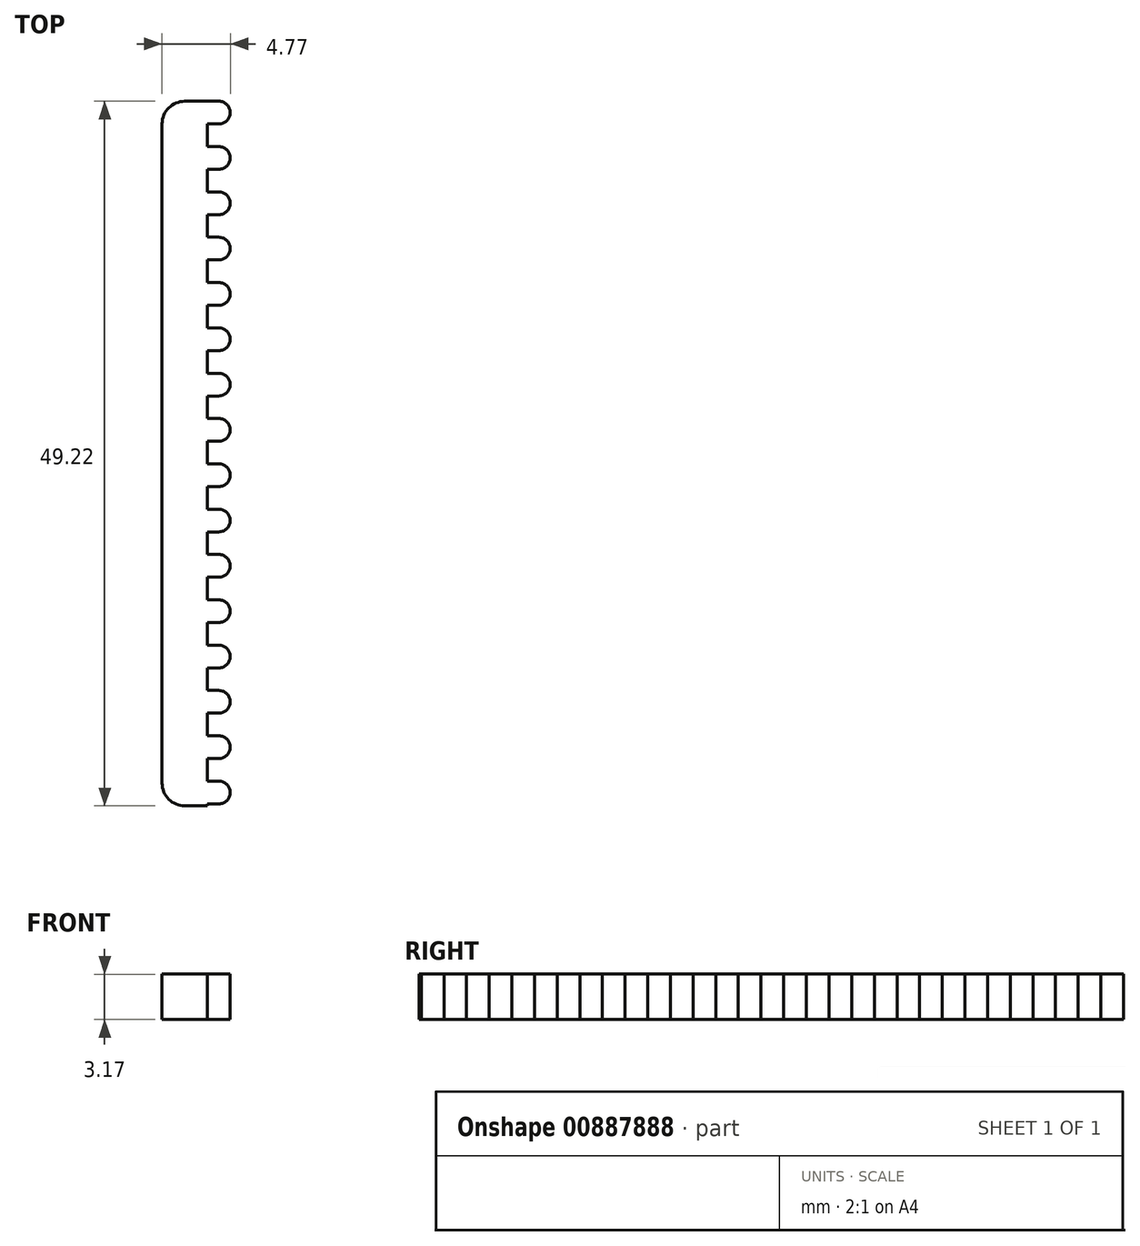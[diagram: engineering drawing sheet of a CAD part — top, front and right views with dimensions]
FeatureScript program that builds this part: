
annotation { "Feature Type Name" : "Feature", "Feature Type Description" : "" }
export const myFeature = defineFeature(function(context is Context, id is Id, definition is map)
    precondition{}
    {
        {
            var Q0;
            Q0=qCreatedBy(makeId("Top.planeOp"),FACE);
            var sketch = newSketch(context, id + "F0", { "sketchPlane" : qUnion([Q0])});
            skLineSegment(sketch, "E0.bottom", {"start": v(-12.7, -24.6) * mm, "end": v(-15.88, -24.6) * mm});
            skLineSegment(sketch, "E0.top", {"start": v(-12.7, 24.6) * mm, "end": v(-15.88, 24.6) * mm});
            skLineSegment(sketch, "E0.left", {"start": v(-12.7, -24.6) * mm, "end": v(-12.7, 24.6) * mm});
            skLineSegment(sketch, "E0.right", {"start": v(-15.88, -24.6) * mm, "end": v(-15.88, 24.6) * mm});
            skPoint(sketch, "E0.middle", {"position": v(-14.29, 0) * mm});
            skLineSegment(sketch, "E1.bottom", {"start": v(-12.7, 24.6) * mm, "end": v(-11.9, 24.6) * mm});
            skLineSegment(sketch, "E1.top", {"start": v(-12.7, 23.02) * mm, "end": v(-11.9, 23.02) * mm});
            skLineSegment(sketch, "E1.left", {"start": v(-12.7, 24.6) * mm, "end": v(-12.7, 23.02) * mm});
            skLineSegment(sketch, "E1.right", {"start": v(-11.11, 23.81) * mm, "end": v(-11.11, 23.81) * mm});
            skPoint(sketch, "E2.visualSharp", {"position": v(-11.11, 24.6) * mm});
            skArc(sketch, "E2.filletArc", {"start": v(-11.11, 23.81) * mm, "mid": v(-11.34, 24.37) * mm, "end": v(-11.9, 24.6) * mm});
            skPoint(sketch, "E3.visualSharp", {"position": v(-11.11, 23.02) * mm});
            skArc(sketch, "E3.filletArc", {"start": v(-11.9, 23.02) * mm, "mid": v(-11.34, 23.25) * mm, "end": v(-11.11, 23.81) * mm});
            skLineSegment(sketch, "E4.1.0.0", {"start": v(-12.7, 21.44) * mm, "end": v(-11.9, 21.44) * mm});
            skArc(sketch, "E4.1.0.1", {"start": v(-11.11, 20.65) * mm, "mid": v(-11.34, 21.2) * mm, "end": v(-11.9, 21.44) * mm});
            skArc(sketch, "E4.1.0.2", {"start": v(-11.9, 19.85) * mm, "mid": v(-11.34, 20.09) * mm, "end": v(-11.11, 20.65) * mm});
            skLineSegment(sketch, "E4.1.0.3", {"start": v(-12.7, 19.85) * mm, "end": v(-11.9, 19.85) * mm});
            skLineSegment(sketch, "E4.2.0.0", {"start": v(-12.7, 18.28) * mm, "end": v(-11.9, 18.28) * mm});
            skArc(sketch, "E4.2.0.1", {"start": v(-11.11, 17.48) * mm, "mid": v(-11.34, 18.04) * mm, "end": v(-11.9, 18.28) * mm});
            skArc(sketch, "E4.2.0.2", {"start": v(-11.9, 16.69) * mm, "mid": v(-11.34, 16.92) * mm, "end": v(-11.11, 17.48) * mm});
            skLineSegment(sketch, "E4.2.0.3", {"start": v(-12.7, 16.69) * mm, "end": v(-11.9, 16.69) * mm});
            skLineSegment(sketch, "E4.3.0.0", {"start": v(-12.7, 15.1) * mm, "end": v(-11.9, 15.1) * mm});
            skArc(sketch, "E4.3.0.1", {"start": v(-11.11, 14.32) * mm, "mid": v(-11.34, 14.88) * mm, "end": v(-11.9, 15.1) * mm});
            skArc(sketch, "E4.3.0.2", {"start": v(-11.9, 13.52) * mm, "mid": v(-11.34, 13.75) * mm, "end": v(-11.11, 14.32) * mm});
            skLineSegment(sketch, "E4.3.0.3", {"start": v(-12.7, 13.52) * mm, "end": v(-11.9, 13.52) * mm});
            skLineSegment(sketch, "E4.4.0.0", {"start": v(-12.7, 11.94) * mm, "end": v(-11.9, 11.94) * mm});
            skArc(sketch, "E4.4.0.1", {"start": v(-11.11, 11.15) * mm, "mid": v(-11.34, 11.71) * mm, "end": v(-11.9, 11.94) * mm});
            skArc(sketch, "E4.4.0.2", {"start": v(-11.9, 10.36) * mm, "mid": v(-11.34, 10.59) * mm, "end": v(-11.11, 11.15) * mm});
            skLineSegment(sketch, "E4.4.0.3", {"start": v(-12.7, 10.36) * mm, "end": v(-11.9, 10.36) * mm});
            skLineSegment(sketch, "E4.5.0.0", {"start": v(-12.7, 8.78) * mm, "end": v(-11.9, 8.78) * mm});
            skArc(sketch, "E4.5.0.1", {"start": v(-11.11, 7.99) * mm, "mid": v(-11.34, 8.55) * mm, "end": v(-11.9, 8.78) * mm});
            skArc(sketch, "E4.5.0.2", {"start": v(-11.9, 7.2) * mm, "mid": v(-11.34, 7.42) * mm, "end": v(-11.11, 7.99) * mm});
            skLineSegment(sketch, "E4.5.0.3", {"start": v(-12.7, 7.2) * mm, "end": v(-11.9, 7.2) * mm});
            skLineSegment(sketch, "E4.6.0.0", {"start": v(-12.7, 5.61) * mm, "end": v(-11.9, 5.61) * mm});
            skArc(sketch, "E4.6.0.1", {"start": v(-11.11, 4.82) * mm, "mid": v(-11.34, 5.38) * mm, "end": v(-11.9, 5.61) * mm});
            skArc(sketch, "E4.6.0.2", {"start": v(-11.9, 4.03) * mm, "mid": v(-11.34, 4.26) * mm, "end": v(-11.11, 4.82) * mm});
            skLineSegment(sketch, "E4.6.0.3", {"start": v(-12.7, 4.03) * mm, "end": v(-11.9, 4.03) * mm});
            skLineSegment(sketch, "E4.7.0.0", {"start": v(-12.7, 2.45) * mm, "end": v(-11.9, 2.45) * mm});
            skArc(sketch, "E4.7.0.1", {"start": v(-11.11, 1.65) * mm, "mid": v(-11.34, 2.22) * mm, "end": v(-11.9, 2.45) * mm});
            skArc(sketch, "E4.7.0.2", {"start": v(-11.9, 0.86) * mm, "mid": v(-11.34, 1.1) * mm, "end": v(-11.11, 1.65) * mm});
            skLineSegment(sketch, "E4.7.0.3", {"start": v(-12.7, 0.86) * mm, "end": v(-11.9, 0.86) * mm});
            skLineSegment(sketch, "E4.8.0.0", {"start": v(-12.7, -0.72) * mm, "end": v(-11.9, -0.72) * mm});
            skArc(sketch, "E4.8.0.1", {"start": v(-11.11, -1.51) * mm, "mid": v(-11.34, -0.95) * mm, "end": v(-11.9, -0.72) * mm});
            skArc(sketch, "E4.8.0.2", {"start": v(-11.9, -2.3) * mm, "mid": v(-11.34, -2.07) * mm, "end": v(-11.11, -1.51) * mm});
            skLineSegment(sketch, "E4.8.0.3", {"start": v(-12.7, -2.3) * mm, "end": v(-11.9, -2.3) * mm});
            skLineSegment(sketch, "E4.9.0.0", {"start": v(-12.7, -3.88) * mm, "end": v(-11.9, -3.88) * mm});
            skArc(sketch, "E4.9.0.1", {"start": v(-11.11, -4.68) * mm, "mid": v(-11.34, -4.12) * mm, "end": v(-11.9, -3.88) * mm});
            skArc(sketch, "E4.9.0.2", {"start": v(-11.9, -5.47) * mm, "mid": v(-11.34, -5.24) * mm, "end": v(-11.11, -4.68) * mm});
            skLineSegment(sketch, "E4.9.0.3", {"start": v(-12.7, -5.47) * mm, "end": v(-11.9, -5.47) * mm});
            skLineSegment(sketch, "E4.10.0.0", {"start": v(-12.7, -7.05) * mm, "end": v(-11.9, -7.05) * mm});
            skArc(sketch, "E4.10.0.1", {"start": v(-11.11, -7.84) * mm, "mid": v(-11.34, -7.28) * mm, "end": v(-11.9, -7.05) * mm});
            skArc(sketch, "E4.10.0.2", {"start": v(-11.9, -8.64) * mm, "mid": v(-11.34, -8.4) * mm, "end": v(-11.11, -7.84) * mm});
            skLineSegment(sketch, "E4.10.0.3", {"start": v(-12.7, -8.64) * mm, "end": v(-11.9, -8.64) * mm});
            skLineSegment(sketch, "E4.11.0.0", {"start": v(-12.7, -10.21) * mm, "end": v(-11.9, -10.21) * mm});
            skArc(sketch, "E4.11.0.1", {"start": v(-11.11, -11) * mm, "mid": v(-11.34, -10.45) * mm, "end": v(-11.9, -10.21) * mm});
            skArc(sketch, "E4.11.0.2", {"start": v(-11.9, -11.8) * mm, "mid": v(-11.34, -11.57) * mm, "end": v(-11.11, -11) * mm});
            skLineSegment(sketch, "E4.11.0.3", {"start": v(-12.7, -11.8) * mm, "end": v(-11.9, -11.8) * mm});
            skLineSegment(sketch, "E4.12.0.0", {"start": v(-12.7, -13.38) * mm, "end": v(-11.9, -13.38) * mm});
            skArc(sketch, "E4.12.0.1", {"start": v(-11.11, -14.17) * mm, "mid": v(-11.34, -13.61) * mm, "end": v(-11.9, -13.38) * mm});
            skArc(sketch, "E4.12.0.2", {"start": v(-11.9, -14.97) * mm, "mid": v(-11.34, -14.73) * mm, "end": v(-11.11, -14.17) * mm});
            skLineSegment(sketch, "E4.12.0.3", {"start": v(-12.7, -14.97) * mm, "end": v(-11.9, -14.97) * mm});
            skLineSegment(sketch, "E4.13.0.0", {"start": v(-12.7, -16.55) * mm, "end": v(-11.9, -16.55) * mm});
            skArc(sketch, "E4.13.0.1", {"start": v(-11.11, -17.34) * mm, "mid": v(-11.34, -16.78) * mm, "end": v(-11.9, -16.55) * mm});
            skArc(sketch, "E4.13.0.2", {"start": v(-11.9, -18.13) * mm, "mid": v(-11.34, -17.9) * mm, "end": v(-11.11, -17.34) * mm});
            skLineSegment(sketch, "E4.13.0.3", {"start": v(-12.7, -18.13) * mm, "end": v(-11.9, -18.13) * mm});
            skLineSegment(sketch, "E4.14.0.0", {"start": v(-12.7, -19.71) * mm, "end": v(-11.9, -19.71) * mm});
            skArc(sketch, "E4.14.0.1", {"start": v(-11.11, -20.5) * mm, "mid": v(-11.34, -19.94) * mm, "end": v(-11.9, -19.71) * mm});
            skArc(sketch, "E4.14.0.2", {"start": v(-11.9, -21.3) * mm, "mid": v(-11.34, -21.07) * mm, "end": v(-11.11, -20.5) * mm});
            skLineSegment(sketch, "E4.14.0.3", {"start": v(-12.7, -21.3) * mm, "end": v(-11.9, -21.3) * mm});
            skLineSegment(sketch, "E4.15.0.0", {"start": v(-12.7, -22.88) * mm, "end": v(-11.9, -22.88) * mm});
            skArc(sketch, "E4.15.0.1", {"start": v(-11.11, -23.67) * mm, "mid": v(-11.34, -23.1) * mm, "end": v(-11.9, -22.88) * mm});
            skArc(sketch, "E4.15.0.2", {"start": v(-11.9, -24.46) * mm, "mid": v(-11.34, -24.23) * mm, "end": v(-11.11, -23.67) * mm});
            skLineSegment(sketch, "E4.15.0.3", {"start": v(-12.7, -24.46) * mm, "end": v(-11.9, -24.46) * mm});
            skLineSegment(sketch, "E4.direction1", {"start": v(-12.7, 24.6) * mm, "end": v(-12.7, 21.44) * mm, "construction": true});
            skSolve(sketch);
        }
        {
            var Q0;
            {var subQ16=sQuery(id+"F0.wireOp",EDGE,"E0.bottom");Q0=makeQuery(id+"F0.imprint","IMPRINT",FACE,{"disambiguationData":[TD([[makeQuery(id+"F0.imprint","IMPRINT",EDGE,{"derivedFrom":subQ16}),-1.0]])]});}
            var Q1;
            {var subQ0=sQuery(id+"F0.wireOp",EDGE,"E4.15.0.0");Q1=makeQuery(id+"F0.imprint","IMPRINT",FACE,{"disambiguationData":[TD([[makeQuery(id+"F0.imprint","IMPRINT",EDGE,{"derivedFrom":subQ0}),-1.0]])]});}
            var Q2;
            {var subQ0=sQuery(id+"F0.wireOp",EDGE,"E4.14.0.0");Q2=makeQuery(id+"F0.imprint","IMPRINT",FACE,{"disambiguationData":[TD([[makeQuery(id+"F0.imprint","IMPRINT",EDGE,{"derivedFrom":subQ0}),-1.0]])]});}
            var Q3;
            {var subQ0=sQuery(id+"F0.wireOp",EDGE,"E4.13.0.0");Q3=makeQuery(id+"F0.imprint","IMPRINT",FACE,{"disambiguationData":[TD([[makeQuery(id+"F0.imprint","IMPRINT",EDGE,{"derivedFrom":subQ0}),-1.0]])]});}
            var Q4;
            {var subQ0=sQuery(id+"F0.wireOp",EDGE,"E4.12.0.0");Q4=makeQuery(id+"F0.imprint","IMPRINT",FACE,{"disambiguationData":[TD([[makeQuery(id+"F0.imprint","IMPRINT",EDGE,{"derivedFrom":subQ0}),-1.0]])]});}
            var Q5;
            {var subQ0=sQuery(id+"F0.wireOp",EDGE,"E4.11.0.0");Q5=makeQuery(id+"F0.imprint","IMPRINT",FACE,{"disambiguationData":[TD([[makeQuery(id+"F0.imprint","IMPRINT",EDGE,{"derivedFrom":subQ0}),-1.0]])]});}
            var Q6;
            {var subQ0=sQuery(id+"F0.wireOp",EDGE,"E4.10.0.0");Q6=makeQuery(id+"F0.imprint","IMPRINT",FACE,{"disambiguationData":[TD([[makeQuery(id+"F0.imprint","IMPRINT",EDGE,{"derivedFrom":subQ0}),-1.0]])]});}
            var Q7;
            {var subQ0=sQuery(id+"F0.wireOp",EDGE,"E4.9.0.0");Q7=makeQuery(id+"F0.imprint","IMPRINT",FACE,{"disambiguationData":[TD([[makeQuery(id+"F0.imprint","IMPRINT",EDGE,{"derivedFrom":subQ0}),-1.0]])]});}
            var Q8;
            {var subQ0=sQuery(id+"F0.wireOp",EDGE,"E4.8.0.0");Q8=makeQuery(id+"F0.imprint","IMPRINT",FACE,{"disambiguationData":[TD([[makeQuery(id+"F0.imprint","IMPRINT",EDGE,{"derivedFrom":subQ0}),-1.0]])]});}
            var Q9;
            {var subQ0=sQuery(id+"F0.wireOp",EDGE,"E4.7.0.0");Q9=makeQuery(id+"F0.imprint","IMPRINT",FACE,{"disambiguationData":[TD([[makeQuery(id+"F0.imprint","IMPRINT",EDGE,{"derivedFrom":subQ0}),-1.0]])]});}
            var Q10;
            {var subQ0=sQuery(id+"F0.wireOp",EDGE,"E4.6.0.0");Q10=makeQuery(id+"F0.imprint","IMPRINT",FACE,{"disambiguationData":[TD([[makeQuery(id+"F0.imprint","IMPRINT",EDGE,{"derivedFrom":subQ0}),-1.0]])]});}
            var Q11;
            {var subQ0=sQuery(id+"F0.wireOp",EDGE,"E4.5.0.0");Q11=makeQuery(id+"F0.imprint","IMPRINT",FACE,{"disambiguationData":[TD([[makeQuery(id+"F0.imprint","IMPRINT",EDGE,{"derivedFrom":subQ0}),-1.0]])]});}
            var Q12;
            {var subQ0=sQuery(id+"F0.wireOp",EDGE,"E4.4.0.0");Q12=makeQuery(id+"F0.imprint","IMPRINT",FACE,{"disambiguationData":[TD([[makeQuery(id+"F0.imprint","IMPRINT",EDGE,{"derivedFrom":subQ0}),-1.0]])]});}
            var Q13;
            {var subQ0=sQuery(id+"F0.wireOp",EDGE,"E4.3.0.0");Q13=makeQuery(id+"F0.imprint","IMPRINT",FACE,{"disambiguationData":[TD([[makeQuery(id+"F0.imprint","IMPRINT",EDGE,{"derivedFrom":subQ0}),-1.0]])]});}
            var Q14;
            {var subQ0=sQuery(id+"F0.wireOp",EDGE,"E4.2.0.0");Q14=makeQuery(id+"F0.imprint","IMPRINT",FACE,{"disambiguationData":[TD([[makeQuery(id+"F0.imprint","IMPRINT",EDGE,{"derivedFrom":subQ0}),-1.0]])]});}
            var Q15;
            {var subQ0=sQuery(id+"F0.wireOp",EDGE,"E4.1.0.0");Q15=makeQuery(id+"F0.imprint","IMPRINT",FACE,{"disambiguationData":[TD([[makeQuery(id+"F0.imprint","IMPRINT",EDGE,{"derivedFrom":subQ0}),-1.0]])]});}
            var Q16;
            Q16=makeQuery(id+"F0.imprint","IMPRINT",FACE,{"disambiguationData":[TD([[makeQuery(id+"F0.imprint","IMPRINT",EDGE,{"derivedFrom":sQuery(id+"F0.wireOp",EDGE,"E1.bottom")}),-1.0]])]});
            extrude(context, id + "F1", {"entities" : qUnion([Q0, Q1, Q2, Q3, Q4, Q5, Q6, Q7, Q8, Q9, Q10, Q11, Q12, Q13, Q14, Q15, Q16]), "depth" : 3.17 * mm, "offsetDistance" : 25.4 * mm});
        }
        {
            var Q0;
            Q0=makeQuery(id+"F1.opExtrude","SWEPT_EDGE",EDGE,{"disambiguationData":[OSD([sQuery(id+"F0.wireOp",EDGE,"E0.top"),sQuery(id+"F0.wireOp",EDGE,"E0.right")])]});
            var Q1;
            Q1=makeQuery(id+"F1.opExtrude","SWEPT_EDGE",EDGE,{"disambiguationData":[OSD([sQuery(id+"F0.wireOp",EDGE,"E0.bottom"),sQuery(id+"F0.wireOp",EDGE,"E0.right")])]});
            fillet(context, id + "F2", {"entities" : qUnion([Q0, Q1]), "radius" : 1.59 * mm, "tangentPropagation" : true, "allowEdgeOverflow" : false});
        }
    });
